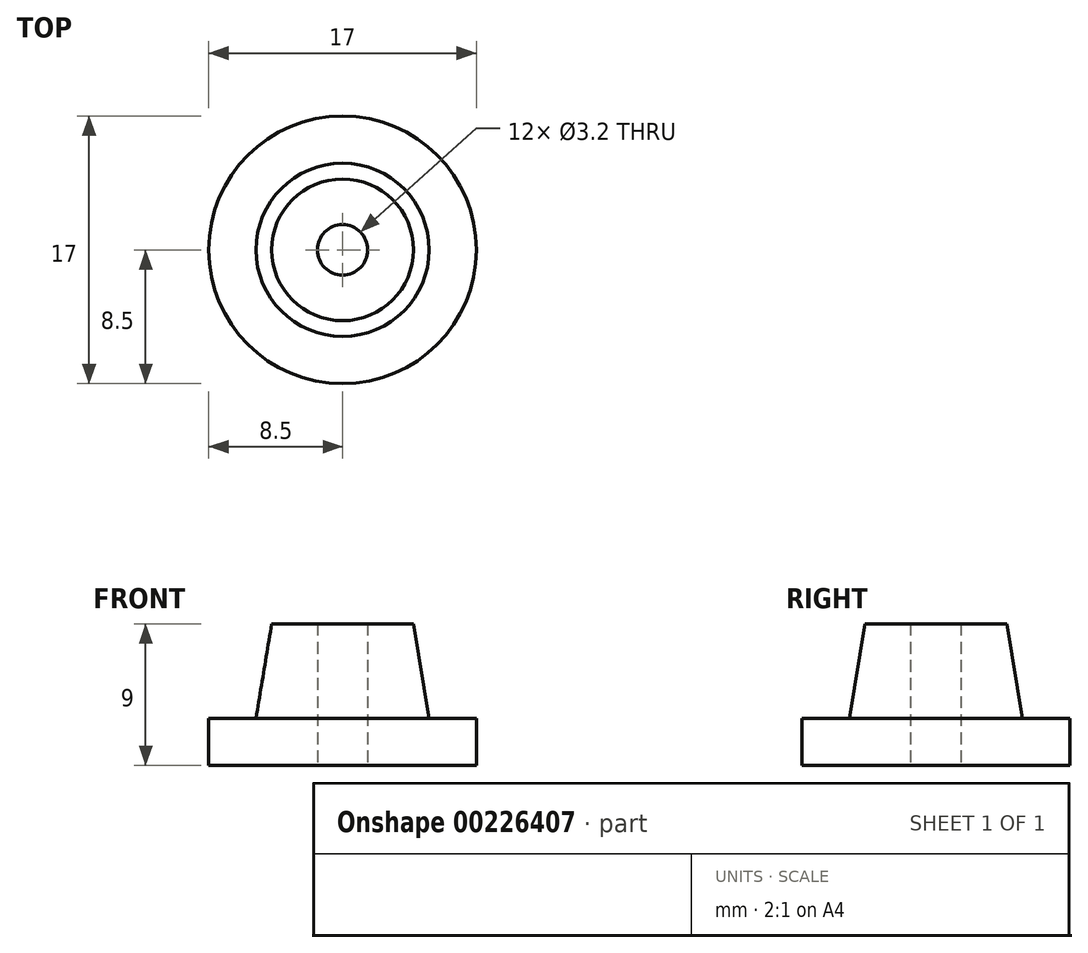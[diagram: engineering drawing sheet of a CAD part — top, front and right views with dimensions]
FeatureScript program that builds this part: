
annotation { "Feature Type Name" : "Feature", "Feature Type Description" : "" }
export const myFeature = defineFeature(function(context is Context, id is Id, definition is map)
    precondition{}
    {
        {
            var Q0;
            Q0=qCreatedBy(makeId("Front.planeOp"),FACE);
            var sketch = newSketch(context, id + "F0", { "sketchPlane" : qUnion([Q0])});
            skLineSegment(sketch, "E0", {"start": v(-1.6, 0) * mm, "end": v(-1.6, 9) * mm});
            skLineSegment(sketch, "E1", {"start": v(-1.6, 9) * mm, "end": v(-4.5, 9) * mm});
            skLineSegment(sketch, "E2", {"start": v(-4.5, 9) * mm, "end": v(-5.5, 3) * mm});
            skLineSegment(sketch, "E3", {"start": v(-5.5, 3) * mm, "end": v(-8.5, 3) * mm});
            skLineSegment(sketch, "E4", {"start": v(-8.5, 3) * mm, "end": v(-8.5, 0) * mm});
            skLineSegment(sketch, "E5", {"start": v(-8.5, 0) * mm, "end": v(-1.6, 0) * mm});
            skLineSegment(sketch, "E6", {"start": v(0, 0) * mm, "end": v(0, 12.68) * mm, "construction": true});
            skSolve(sketch);
        }
        {
            var Q0;
            Q0=makeQuery(id+"F0.imprint","IMPRINT",FACE,{"disambiguationData":[TD([[makeQuery(id+"F0.imprint","IMPRINT",EDGE,{"derivedFrom":sQuery(id+"F0.wireOp",EDGE,"E0")}),1.0]])]});
            var Q1;
            Q1=sQuery(id+"F0.wireOp",EDGE,"E6");
            var Q2;
            Q2=sQuery(id+"F0.wireOp",EDGE,"E6");
            revolve(context, id + "F1", {"entities" : qUnion([Q0]), "surfaceEntities" : qUnion([Q1]), "axis" : qUnion([Q2]), "revolveType" : RevolveType.FULL});
        }
    });
